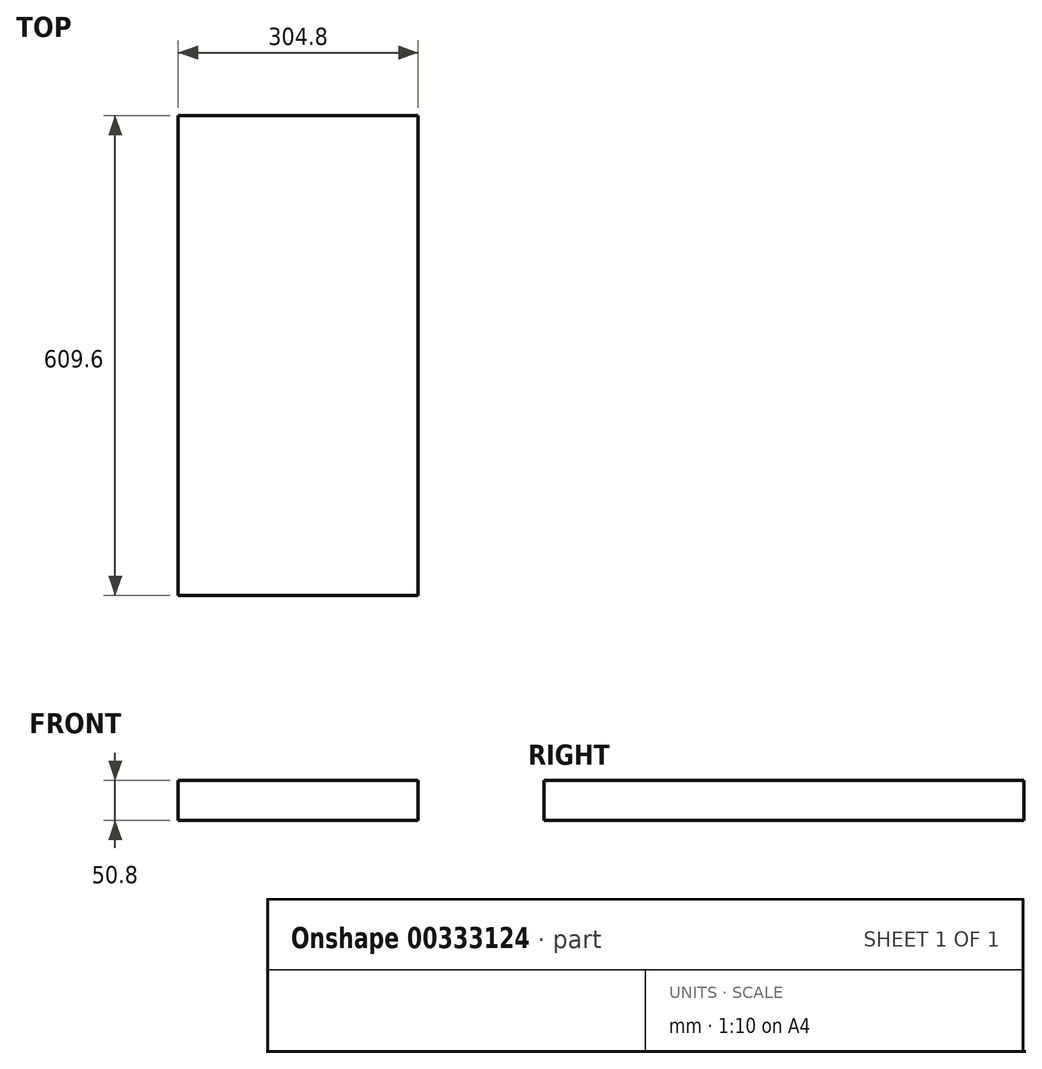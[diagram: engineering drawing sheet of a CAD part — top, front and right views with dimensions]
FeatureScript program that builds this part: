
annotation { "Feature Type Name" : "Feature", "Feature Type Description" : "" }
export const myFeature = defineFeature(function(context is Context, id is Id, definition is map)
    precondition{}
    {
        {
            var Q0;
            Q0=qCreatedBy(makeId("Top.planeOp"),FACE);
            var sketch = newSketch(context, id + "F0", { "sketchPlane" : qUnion([Q0])});
            skLineSegment(sketch, "E0.bottom", {"start": v(0, 0) * mm, "end": v(304.8, 0) * mm});
            skLineSegment(sketch, "E0.top", {"start": v(0, 609.6) * mm, "end": v(304.8, 609.6) * mm});
            skLineSegment(sketch, "E0.left", {"start": v(0, 0) * mm, "end": v(0, 609.6) * mm});
            skLineSegment(sketch, "E0.right", {"start": v(304.8, 0) * mm, "end": v(304.8, 609.6) * mm});
            skSolve(sketch);
        }
        {
            var Q0;
            Q0 = qSketchRegion(id + "F0", true);
            extrude(context, id + "F1", {"entities" : qUnion([Q0]), "depth" : 50.8 * mm});
        }
    });
